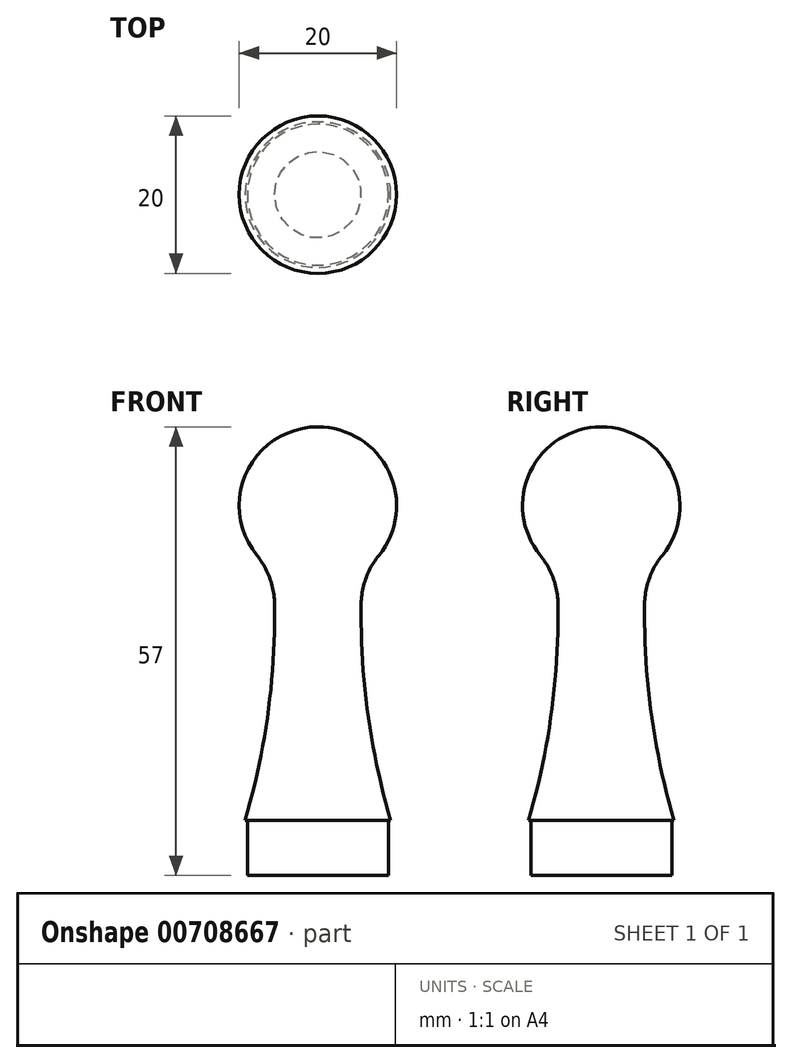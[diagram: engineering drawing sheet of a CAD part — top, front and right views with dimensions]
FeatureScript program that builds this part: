
annotation { "Feature Type Name" : "Feature", "Feature Type Description" : "" }
export const myFeature = defineFeature(function(context is Context, id is Id, definition is map)
    precondition{}
    {
        {
            var Q0;
            Q0=qCreatedBy(makeId("Front.planeOp"),FACE);
            var sketch = newSketch(context, id + "F0", { "sketchPlane" : qUnion([Q0])});
            skLineSegment(sketch, "E0", {"start": v(0, 0) * mm, "end": v(0, 108.44) * mm, "construction": true});
            skLineSegment(sketch, "E1", {"start": v(-9.25, 0) * mm, "end": v(-8.95, 0) * mm});
            skArc(sketch, "E2", {"start": v(0, 50) * mm, "mid": v(-9.55, 42.96) * mm, "end": v(-5.66, 31.76) * mm});
            skArc(sketch, "E3", {"start": v(-9.25, 0) * mm, "mid": v(-6.08, 15.72) * mm, "end": v(-5.66, 31.76) * mm});
            skLineSegment(sketch, "E4", {"start": v(0, 50) * mm, "end": v(0, 0) * mm});
            skLineSegment(sketch, "E5", {"start": v(-8.95, 0) * mm, "end": v(-8.95, -7) * mm});
            skLineSegment(sketch, "E6", {"start": v(-8.95, -7) * mm, "end": v(0, -7) * mm});
            skLineSegment(sketch, "E7", {"start": v(0, -7) * mm, "end": v(0, 0) * mm});
            skSolve(sketch);
        }
        {
            var Q0;
            Q0=makeQuery(id+"F0.imprint","IMPRINT",FACE,{"disambiguationData":[TD([[makeQuery(id+"F0.imprint","IMPRINT",EDGE,{"derivedFrom":sQuery(id+"F0.wireOp",EDGE,"E1")}),1.0]])]});
            var Q1;
            Q1=sQuery(id+"F0.wireOp",EDGE,"E0");
            revolve(context, id + "F1", {"surfaceOperationType" : NewSurfaceOperationType.NEW, "entities" : qUnion([Q0]), "axis" : qUnion([Q1]), "revolveType" : RevolveType.FULL});
        }
        {
            var Q0;
            Q0=makeQuery(id+"F1.opRevolve","SWEPT_EDGE",EDGE,{"disambiguationData":[OSD([sQuery(id+"F0.wireOp",EDGE,"E2"),sQuery(id+"F0.wireOp",EDGE,"E3")])]});
            fillet(context, id + "F2", {"entities" : qUnion([Q0]), "radius" : 10 * mm, "tangentPropagation" : true, "allowEdgeOverflow" : false});
        }
    });
